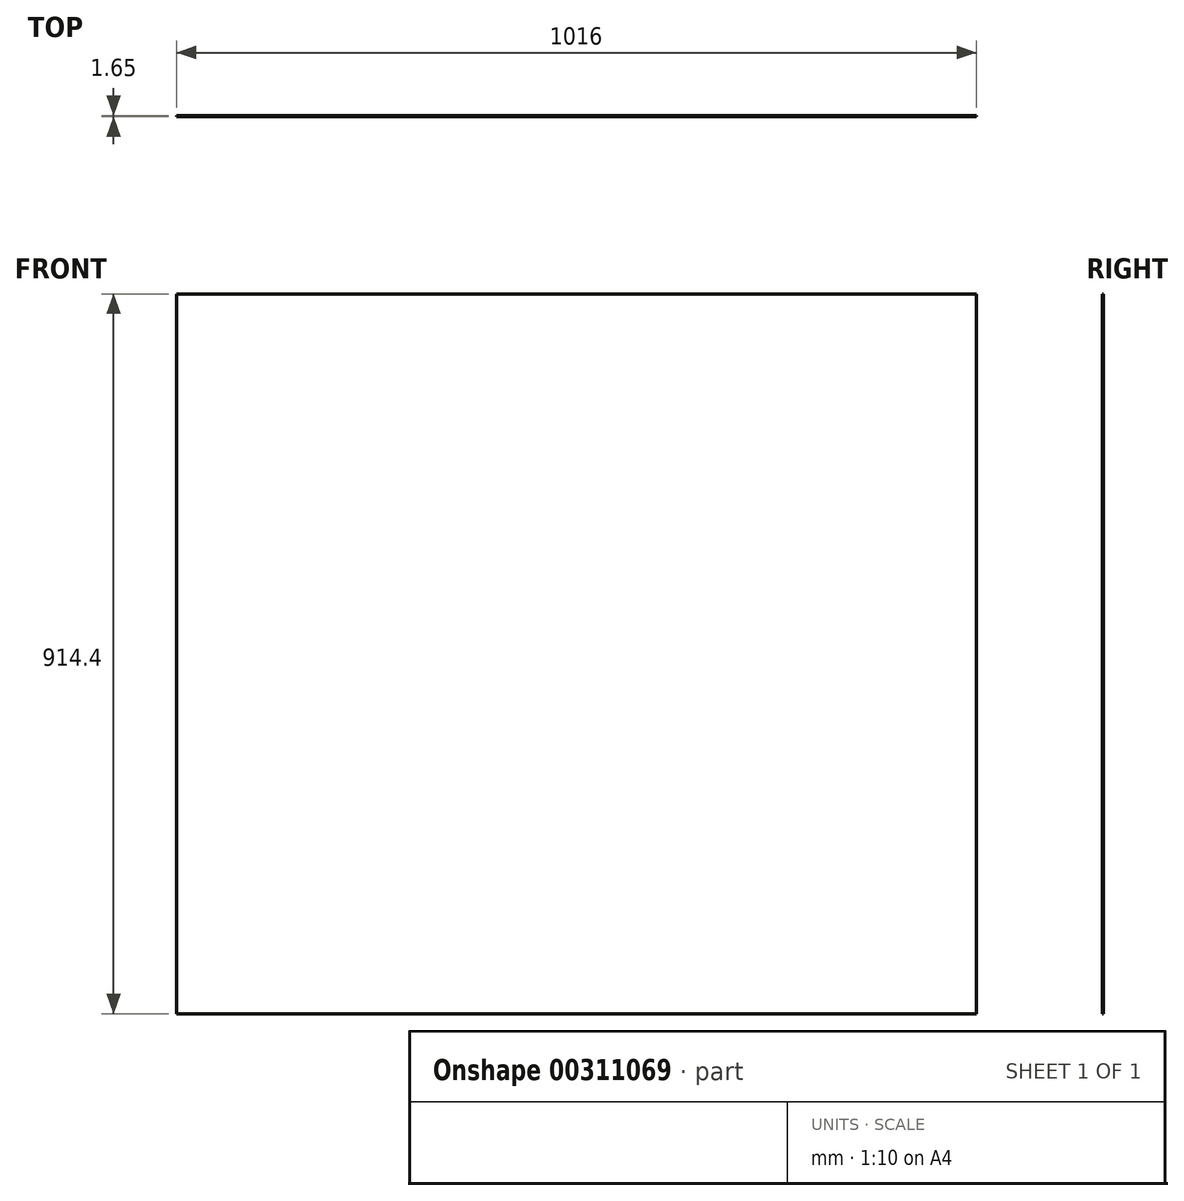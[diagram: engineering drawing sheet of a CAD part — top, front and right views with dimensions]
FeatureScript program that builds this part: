
annotation { "Feature Type Name" : "Feature", "Feature Type Description" : "" }
export const myFeature = defineFeature(function(context is Context, id is Id, definition is map)
    precondition{}
    {
        {
            var Q0;
            Q0=qCreatedBy(makeId("Front.planeOp"),FACE);
            var sketch = newSketch(context, id + "F0", { "sketchPlane" : qUnion([Q0])});
            skLineSegment(sketch, "E0.bottom", {"start": v(0, 0) * mm, "end": v(1016, 0) * mm});
            skLineSegment(sketch, "E0.top", {"start": v(0, 914.4) * mm, "end": v(1016, 914.4) * mm});
            skLineSegment(sketch, "E0.left", {"start": v(0, 0) * mm, "end": v(0, 914.4) * mm});
            skLineSegment(sketch, "E0.right", {"start": v(1016, 0) * mm, "end": v(1016, 914.4) * mm});
            skSolve(sketch);
        }
        {
            var Q0;
            Q0 = qSketchRegion(id + "F0", true);
            extrude(context, id + "F1", {"entities" : qUnion([Q0]), "depth" : 1.65 * mm});
        }
    });
